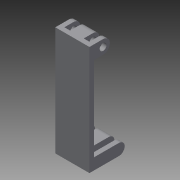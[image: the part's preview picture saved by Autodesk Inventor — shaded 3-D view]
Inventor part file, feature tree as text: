
AUTODESK INVENTOR PART (.ipt)
format: ipt  version: 2015 (Build 190159000, 159)  size: 217,600 bytes
history: native  units: mm
features: extrude x9, sketch x9, mirror x6, plane x3
ambient origin geometry x8: Origin, YZ Plane, XZ Plane, XY Plane, X Axis, Y Axis, Z Axis, Center Point
bodies: Solid1 (feature_tree)
feature tree (27):
  extrude  "Extrusion1"  Depth=15.0mm
  extrude  "Extrusion2"  Depth=5.0mm
  plane  "Work Plane1"
  mirror  "Mirror1"
  plane  "Work Plane2"
  mirror  "Mirror2"
  extrude  "Extrusion3"  Depth=10.0mm TaperAngle=0.0deg
  mirror  "Mirror3"
  extrude  "Extrusion4"  [1 undecoded]
  mirror  "Mirror4"
  mirror  "Mirror5"
  extrude  "Extrusion5"  Depth=45.0mm
  extrude  "Extrusion6"  Depth=3.0mm
  mirror  "Mirror6"
  extrude  "Extrusion7"  Depth=2.0mm TaperAngle=0.0deg
  extrude  "Extrusion8"  Depth=2.0mm TaperAngle=0.0deg
  plane  "Work Plane3"
  extrude  "Extrusion9"  Depth=1.0mm TaperAngle=0.0deg
  sketch  "Sketch1"  dims[d0=15.0mm d1=120.0mm]
  sketch  "Sketch3"  dims[d2=3.0mm d3=0.0mm d4=5.0mm]
  sketch  "Sketch6"  dims[d5=10.0mm d6=2.0mm d7=0.0mm]
  sketch  "Sketch9"  dims[d8=-7.5mm d10=-4.25mm]
  sketch  "Sketch10"  dims[d13=2.0mm d14=0.0mm d16=45.0mm]
  sketch  "Sketch11"  dims[d17=3.0mm d18=3.0mm]
  sketch  "Sketch12"  dims[d20=3.0mm d21=2.0mm d22=0.0mm]
  sketch  "Sketch13"  dims[d23=2.0mm d24=0.0mm d25=2.0mm d26=0.0mm]
  sketch  "Sketch15"  dims[d27=3.0mm d28=0.0mm d29=1.0mm d30=0.0mm d31=7.0mm d32=1.6mm d33=3.0mm d34=0.0mm]
note: 1 required parameter value undecoded (feature->parameter linkage not recoverable at this tier; creation-order binding heuristic only, values carry confidence <= 0.55)
